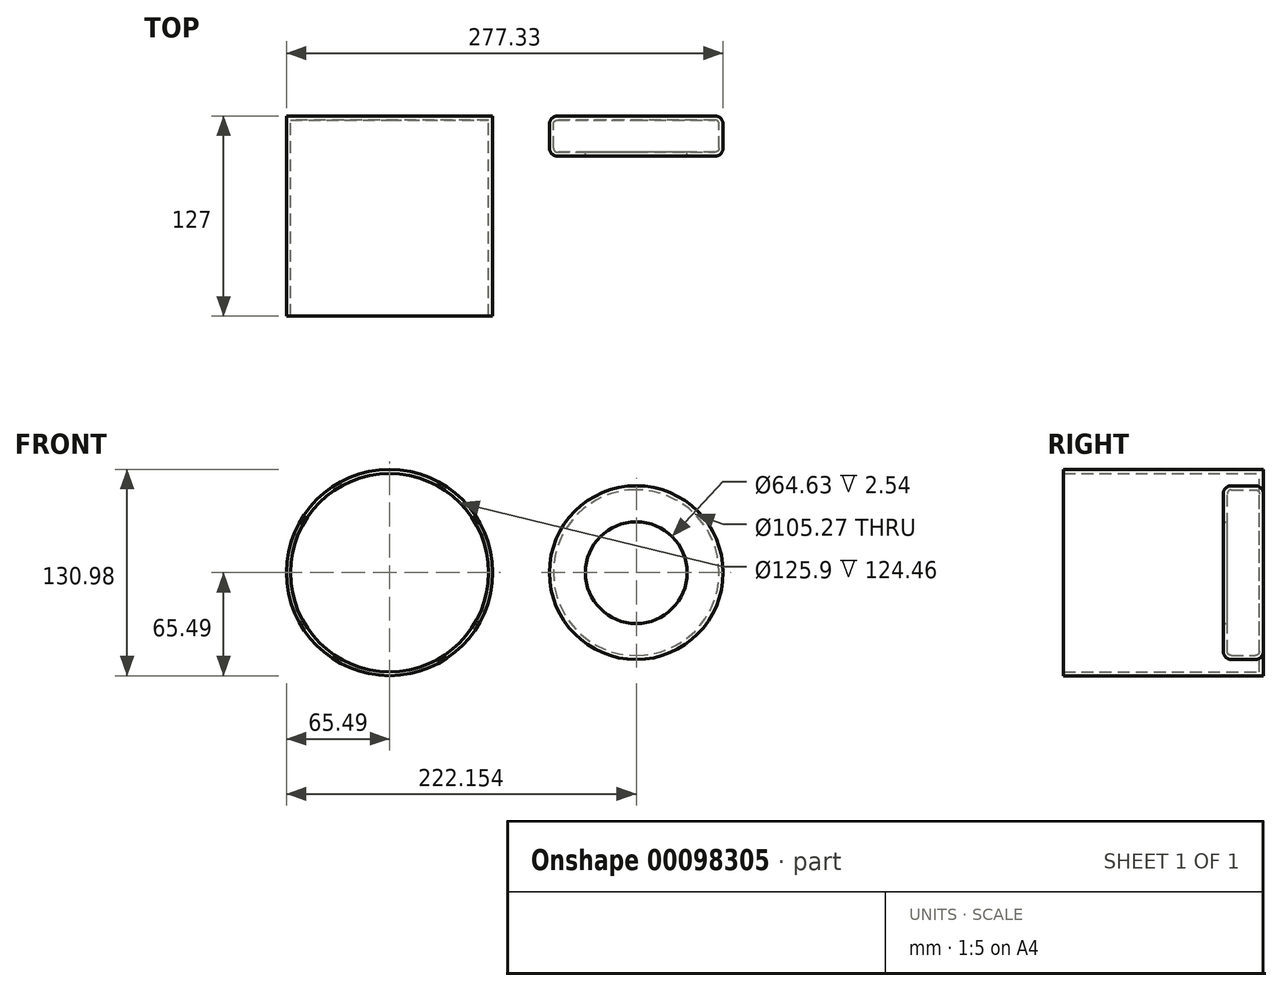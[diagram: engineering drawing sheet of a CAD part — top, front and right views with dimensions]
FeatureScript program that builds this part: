
annotation { "Feature Type Name" : "Feature", "Feature Type Description" : "" }
export const myFeature = defineFeature(function(context is Context, id is Id, definition is map)
    precondition{}
    {
        {
            var Q0;
            Q0=qCreatedBy(makeId("Front.planeOp"),FACE);
            var sketch = newSketch(context, id + "F0", { "sketchPlane" : qUnion([Q0])});
            skCircle(sketch, "E0", {"center": v(0, 0) * mm, "radius": 65.49 * mm});
            skSolve(sketch);
        }
        {
            var Q0;
            Q0=makeQuery(id+"F0.imprint","IMPRINT",FACE,{"disambiguationData":[TD([[makeQuery(id+"F0.imprint","IMPRINT",EDGE,{"derivedFrom":sQuery(id+"F0.wireOp",EDGE,"E0")}),1.0]])]});
            extrude(context, id + "F1", {"entities" : qUnion([Q0]), "depth" : 127 * mm});
        }
        {
            var Q0;
            Q0=makeQuery(id+"F1.opExtrude","CAP_FACE",FACE,{"disambiguationData":[OSD([sQuery(id+"F0.wireOp",EDGE,"E0")])],"isStart":false});
            shell(context, id + "F2", {"entities" : qUnion([Q0]), "thickness" : 2.54 * mm});
        }
        {
            var Q0;
            Q0=qCreatedBy(makeId("Front.planeOp"),FACE);
            var sketch = newSketch(context, id + "F10", { "sketchPlane" : qUnion([Q0])});
            skCircle(sketch, "E1", {"center": v(156.66, 0) * mm, "radius": 55.17 * mm});
            skSolve(sketch);
        }
        {
            var Q0;
            Q0=makeQuery(id+"F10.imprint","IMPRINT",FACE,{"disambiguationData":[TD([[makeQuery(id+"F10.imprint","IMPRINT",EDGE,{"derivedFrom":sQuery(id+"F10.wireOp",EDGE,"E1")}),1.0]])]});
            extrude(context, id + "F11", {"entities" : qUnion([Q0]), "depth" : 25.4 * mm});
        }
        {
            var Q0;
            Q0=makeQuery(id+"F11.opExtrude","SWEPT_FACE",FACE,{"disambiguationData":[OSD([sQuery(id+"F10.wireOp",EDGE,"E1")])]});
            fillet(context, id + "F3", {"entities" : qUnion([Q0]), "radius" : 5.08 * mm, "tangentPropagation" : true, "allowEdgeOverflow" : false});
        }
        {
            var Q0;
            Q0=makeQuery(id+"F11.opExtrude","CAP_FACE",FACE,{"disambiguationData":[OSD([sQuery(id+"F10.wireOp",EDGE,"E1")])],"isStart":false});
            shell(context, id + "F4", {"entities" : qUnion([Q0]), "thickness" : 22.86 * mm});
        }
        {
            var Q0;
            {var subQ0=sQuery(id+"F10.wireOp",EDGE,"E1");Q0=makeQuery(id+"F4.opShell","OFFSET_FACE",FACE,{"disambiguationData":[OSD([subQ0]),TDD([makeQuery(id+"F11.opExtrude","CAP_FACE",FACE,{"disambiguationData":[OSD([subQ0])],"isStart":true})])]});}
            shell(context, id + "F5", {"entities" : qUnion([Q0]), "thickness" : 2.54 * mm});
        }
        {
            var Q0;
            Q0=qCreatedBy(makeId("Top.planeOp"),FACE);
            var sketch = newSketch(context, id + "F6", { "sketchPlane" : qUnion([Q0])});
            skCircle(sketch, "E2", {"center": v(0, -26.28) * mm, "radius": 8.6 * mm});
            skSolve(sketch);
        }
        {
            var Q0;
            Q0=sQuery(id+"F6.wireOp",EDGE,"E2");
            extrude(context, id + "F7", {"bodyType" : ToolBodyType.SURFACE, "surfaceEntities" : qUnion([Q0]), "depth" : 202.23 * mm});
        }
    });
